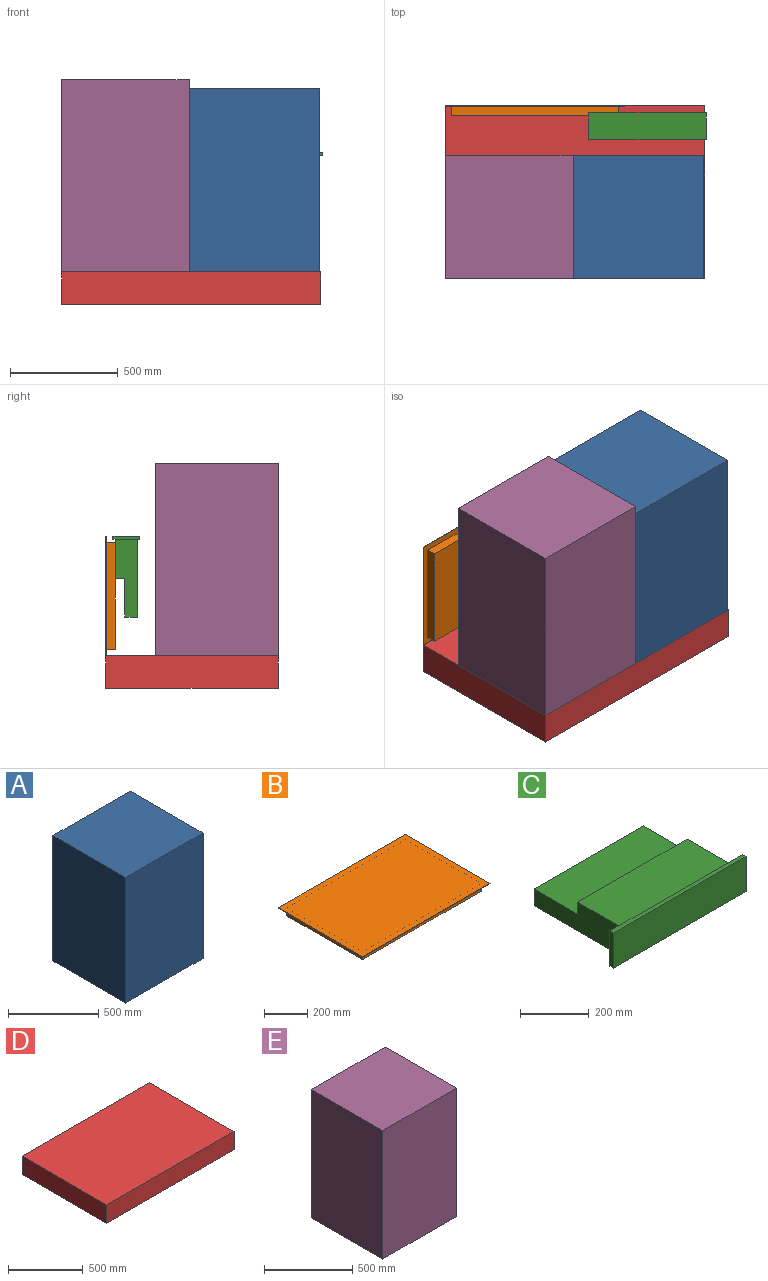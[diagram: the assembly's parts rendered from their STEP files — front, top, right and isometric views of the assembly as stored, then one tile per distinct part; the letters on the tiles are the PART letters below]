
ASSEMBLY  parts=5 mates=10
PART A: 6 faces, bbox 605x570x850 mm
  f0: plane 850x570mm, normal (-1,0,0), area 484500mm2, adj f1,f3,f4,f5
  f1: plane 605x570mm, normal (0,0,-1), area 344850mm2, adj f0,f2,f4,f5
  f2: plane 850x570mm, normal (1,0,0), area 484500mm2, adj f1,f3,f4,f5
  f3: plane 605x570mm, normal (0,0,1), area 344850mm2, adj f0,f2,f4,f5
  f4: plane 850x605mm, normal (0,1,0), area 514250mm2, adj f0,f1,f2,f3
  f5: plane 850x605mm, normal (0,-1,0), area 514250mm2, adj f0,f1,f2,f3
PART B: 11 faces, bbox 830x555x45 mm
  f0: plane 555x3mm, normal (-1,0,0), area 1665mm2, adj f1,f3,f4,f5
  f1: plane 830x3mm, normal (0,-1,0), area 2490mm2, adj f0,f2,f4,f5
  f2: plane 555x3mm, normal (1,0,0), area 1665mm2, adj f1,f3,f4,f5
  f3: plane 830x3mm, normal (0,1,0), area 2490mm2, adj f0,f2,f4,f5
  f4: plane 830x555mm, normal (0,0,1), area 460650mm2, adj f0,f1,f2,f3
  f5: plane 830x555mm, normal (0,0,-1), area 77025mm2, adj f0,f1,f2,f3,f6,f7,f8,f9
  f6: plane 495x42mm, normal (1,0,0), area 20790mm2, adj f5,f7,f9,f10
  f7: plane 775x42mm, normal (0,-1,0), area 32550mm2, adj f5,f6,f8,f10
  f8: plane 495x42mm, normal (-1,0,0), area 20790mm2, adj f5,f7,f9,f10
  f9: plane 775x42mm, normal (0,1,0), area 32550mm2, adj f5,f6,f8,f10
  f10: plane 775x495mm, normal (0,0,-1), area 383625mm2, adj f6,f7,f8,f9
PART C: 13 faces, bbox 545x375x125 mm
  f0: plane 450x43mm, normal (0,1,0), area 19350mm2, adj f7,f8,f9,f11
  f1: plane 125x15mm, normal (-1,0,0), area 1875mm2, adj f2,f4,f5,f6
  f2: plane 545x15mm, normal (0,0,-1), area 8175mm2, adj f1,f3,f5,f6
  f3: plane 125x15mm, normal (1,0,0), area 1875mm2, adj f2,f4,f5,f6
  f4: plane 545x15mm, normal (0,0,1), area 8175mm2, adj f1,f3,f5,f6
  f5: plane 545x125mm, normal (0,-1,0), area 68125mm2, adj f1,f2,f3,f4
  f6: plane 545x125mm, normal (0,1,0), area 21775mm2, adj f1,f2,f3,f4,f7,f8,f9,f10
  f7: plane 360x103mm, normal (-1,0,0), area 29340mm2, adj f0,f6,f8,f10,f11,f12
  f8: plane 450x180mm, normal (0,0,1), area 81000mm2, adj f0,f6,f7,f9
  f9: plane 360x103mm, normal (1,0,0), area 29340mm2, adj f0,f6,f8,f10,f11,f12
  f10: plane 450x360mm, normal (0,0,-1), area 162000mm2, adj f6,f7,f9,f12
  f11: plane 450x180mm, normal (0,0,1), area 81000mm2, adj f0,f7,f9,f12
  f12: plane 450x60mm, normal (0,1,0), area 27000mm2, adj f7,f9,f10,f11
PART D: 6 faces, bbox 1200x800x150 mm
  f0: plane 800x150mm, normal (-1,0,0), area 120000mm2, adj f1,f3,f4,f5
  f1: plane 1200x800mm, normal (0,0,-1), area 960000mm2, adj f0,f2,f4,f5
  f2: plane 800x150mm, normal (1,0,0), area 120000mm2, adj f1,f3,f4,f5
  f3: plane 1200x800mm, normal (0,0,1), area 960000mm2, adj f0,f2,f4,f5
  f4: plane 1200x150mm, normal (0,1,0), area 180000mm2, adj f0,f1,f2,f3
  f5: plane 1200x150mm, normal (0,-1,0), area 180000mm2, adj f0,f1,f2,f3
PART E: 6 faces, bbox 590x570x890 mm
  f0: plane 890x570mm, normal (-1,0,0), area 507300mm2, adj f1,f3,f4,f5
  f1: plane 590x570mm, normal (0,0,-1), area 336300mm2, adj f0,f2,f4,f5
  f2: plane 890x570mm, normal (1,0,0), area 507300mm2, adj f1,f3,f4,f5
  f3: plane 590x570mm, normal (0,0,1), area 336300mm2, adj f0,f2,f4,f5
  f4: plane 890x590mm, normal (0,1,0), area 525100mm2, adj f0,f1,f2,f3
  f5: plane 890x590mm, normal (0,-1,0), area 525100mm2, adj f0,f1,f2,f3
PLACE A t=(1048.44,-267.7,534.41)mm
PLACE B rot(axis=(-1,0,0),90deg) t=(458.37,529.3,1089.41)mm
PLACE C rot(axis=(-1,0,0),90deg) t=(1120.9,373.3,1074.41)mm
PLACE D t=(458.44,-267.7,384.41)mm
PLACE E t=(458.44,-267.7,534.41)mm
MATE planar E.f0 <-> D.f0  axis (-1,0,0) through (458.44,17.3,979.41)mm
MATE planar C.f8 <-> B.f10  axis (0,1,0) through (1393.4,487.3,984.41)mm
MATE planar B.f1 <-> C.f5  axis (0,0,1) through (873.37,530.8,1089.41)mm
MATE planar E.f5 <-> A.f5  axis (0,-1,0) through (753.44,-267.7,979.41)mm
MATE planar A.f1 <-> D.f3  axis (0,0,-1) through (1350.94,17.3,534.41)mm
MATE planar E.f1 <-> D.f3  axis (0,0,-1) through (753.44,17.3,534.41)mm
MATE planar B.f4 <-> D.f4  axis (0,1,0) through (1288.37,532.3,811.91)mm
MATE planar B.f3 <-> D.f3  axis (0,0,-1) through (873.37,530.8,534.41)mm
MATE planar E.f2 <-> A.f0  axis (1,0,0) through (1048.44,302.3,534.41)mm
MATE planar E.f5 <-> D.f5  axis (0,-1,0) through (753.44,-267.7,979.41)mm
